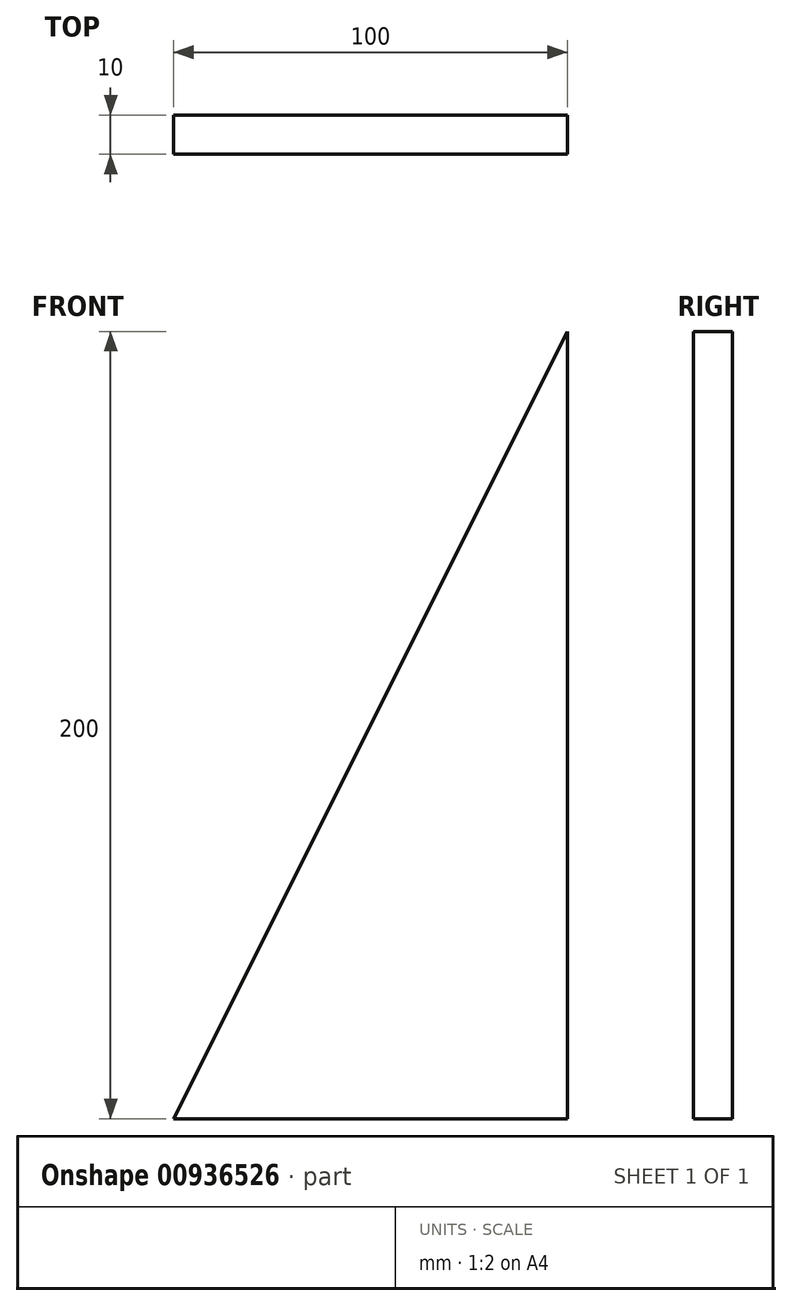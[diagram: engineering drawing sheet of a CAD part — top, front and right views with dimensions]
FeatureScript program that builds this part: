
annotation { "Feature Type Name" : "Feature", "Feature Type Description" : "" }
export const myFeature = defineFeature(function(context is Context, id is Id, definition is map)
    precondition{}
    {
        {
            var Q0;
            Q0=qCreatedBy(makeId("Front.planeOp"),FACE);
            var sketch = newSketch(context, id + "F0", { "sketchPlane" : qUnion([Q0])});
            skLineSegment(sketch, "E0", {"start": v(0, 0) * mm, "end": v(-100, 0) * mm});
            skLineSegment(sketch, "E1", {"start": v(-100, 0) * mm, "end": v(0, 200) * mm});
            skLineSegment(sketch, "E2", {"start": v(0, 200) * mm, "end": v(0, 0) * mm});
            skSolve(sketch);
        }
        {
            var Q0;
            Q0=makeQuery(id+"F0.imprint","IMPRINT",FACE,{"disambiguationData":[TD([[makeQuery(id+"F0.imprint","IMPRINT",EDGE,{"derivedFrom":sQuery(id+"F0.wireOp",EDGE,"E0")}),-1.0]])]});
            extrude(context, id + "F1", {"entities" : qUnion([Q0]), "depth" : 10 * mm, "offsetDistance" : 25 * mm});
        }
    });
